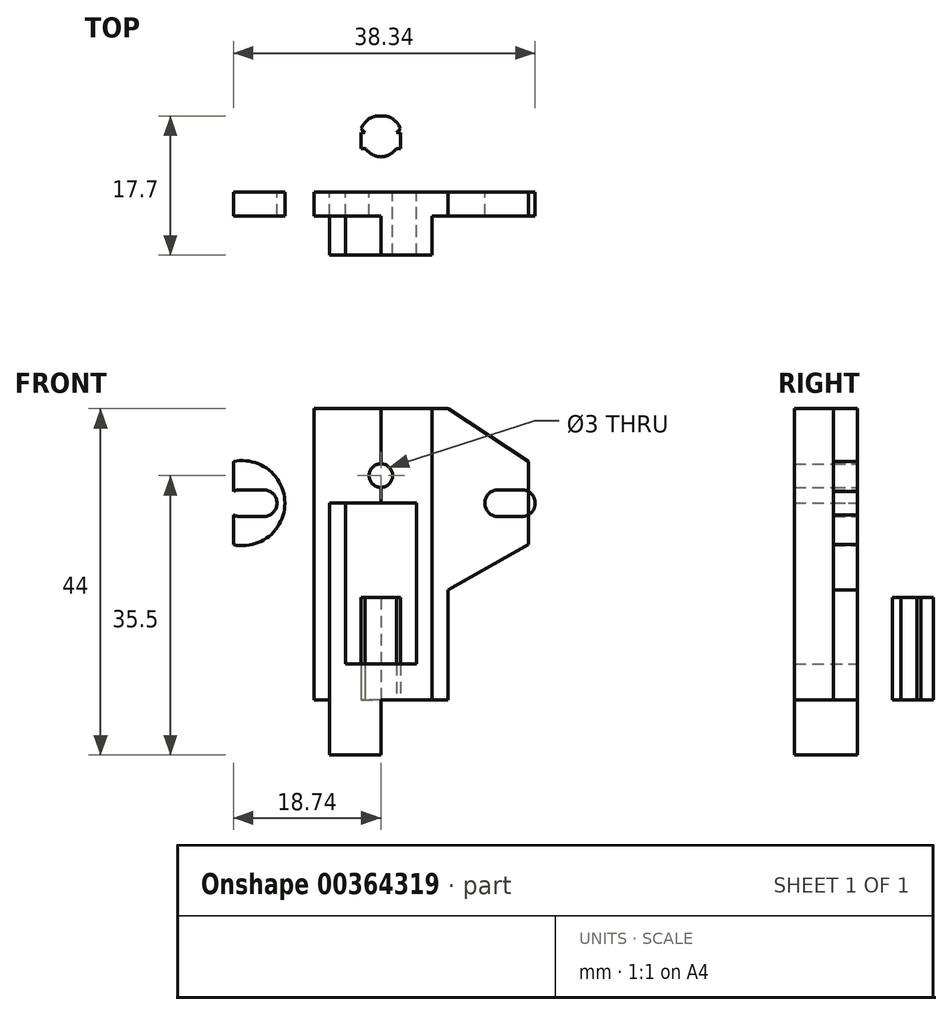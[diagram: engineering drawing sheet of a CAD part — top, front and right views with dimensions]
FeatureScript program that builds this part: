
annotation { "Feature Type Name" : "Feature", "Feature Type Description" : "" }
export const myFeature = defineFeature(function(context is Context, id is Id, definition is map)
    precondition{}
    {
        {
            var Q0;
            Q0=qCreatedBy(makeId("Front.planeOp"),FACE);
            var sketch = newSketch(context, id + "F0", { "sketchPlane" : qUnion([Q0])});
            skLineSegment(sketch, "E0.bottom", {"start": v(0, 0) * mm, "end": v(-8.5, 0) * mm});
            skLineSegment(sketch, "E0.top", {"start": v(0, 37) * mm, "end": v(-8.5, 37) * mm});
            skLineSegment(sketch, "E0.left", {"start": v(0, 0) * mm, "end": v(0, 37) * mm});
            skLineSegment(sketch, "E0.right", {"start": v(-8.5, 0) * mm, "end": v(-8.5, 37) * mm});
            skCircle(sketch, "E1", {"center": v(-17.6, 25) * mm, "radius": 5.4 * mm});
            skLineSegment(sketch, "E2", {"start": v(-8.5, 14) * mm, "end": v(-8.5, 37) * mm});
            skLineSegment(sketch, "E3", {"start": v(-8.5, 37) * mm, "end": v(-18.74, 30.28) * mm});
            skLineSegment(sketch, "E4", {"start": v(-18.74, 30.28) * mm, "end": v(-18.74, 19.72) * mm});
            skLineSegment(sketch, "E5", {"start": v(-18.74, 19.72) * mm, "end": v(-8.5, 14) * mm});
            skLineSegment(sketch, "E6.bottom", {"start": v(0, 37) * mm, "end": v(-6.5, 37) * mm});
            skLineSegment(sketch, "E6.top", {"start": v(0, -7) * mm, "end": v(-6.5, -7) * mm});
            skLineSegment(sketch, "E6.left", {"start": v(0, 37) * mm, "end": v(0, -7) * mm});
            skLineSegment(sketch, "E6.right", {"start": v(-6.5, 37) * mm, "end": v(-6.5, -7) * mm});
            skLineSegment(sketch, "E7.bottom", {"start": v(-6.5, 37) * mm, "end": v(0, 37) * mm});
            skLineSegment(sketch, "E7.top", {"start": v(-6.5, 25) * mm, "end": v(0, 25) * mm});
            skLineSegment(sketch, "E7.left", {"start": v(-6.5, 37) * mm, "end": v(-6.5, 25) * mm});
            skLineSegment(sketch, "E7.right", {"start": v(0, 37) * mm, "end": v(0, 25) * mm});
            skLineSegment(sketch, "E8.bottom", {"start": v(-6.5, -7) * mm, "end": v(0, -7) * mm});
            skLineSegment(sketch, "E8.top", {"start": v(-6.5, 4.6) * mm, "end": v(0, 4.6) * mm});
            skLineSegment(sketch, "E8.left", {"start": v(-6.5, -7) * mm, "end": v(-6.5, 4.6) * mm});
            skLineSegment(sketch, "E8.right", {"start": v(0, -7) * mm, "end": v(0, 4.6) * mm});
            skLineSegment(sketch, "E9.bottom", {"start": v(0, 25) * mm, "end": v(-4.5, 25) * mm});
            skLineSegment(sketch, "E9.top", {"start": v(0, 4.6) * mm, "end": v(-4.5, 4.6) * mm});
            skLineSegment(sketch, "E9.left", {"start": v(0, 25) * mm, "end": v(0, 4.6) * mm});
            skLineSegment(sketch, "E9.right", {"start": v(-4.5, 25) * mm, "end": v(-4.5, 4.6) * mm});
            skLineSegment(sketch, "E10.MirrorCS", {"start": v(6.5, 4.6) * mm, "end": v(0, 4.6) * mm});
            skLineSegment(sketch, "E11.MirrorCS", {"start": v(0, 4.6) * mm, "end": v(4.5, 4.6) * mm});
            skLineSegment(sketch, "E12.MirrorCS", {"start": v(6.5, 37) * mm, "end": v(0, 37) * mm});
            skLineSegment(sketch, "E13.MirrorCS", {"start": v(6.5, 25) * mm, "end": v(0, 25) * mm});
            skLineSegment(sketch, "E14.MirrorCS", {"start": v(0, 25) * mm, "end": v(4.5, 25) * mm});
            skLineSegment(sketch, "E15.MirrorCS", {"start": v(0, 37) * mm, "end": v(8.5, 37) * mm});
            skLineSegment(sketch, "E16.MirrorCS", {"start": v(6.5, -7) * mm, "end": v(6.5, 4.6) * mm});
            skLineSegment(sketch, "E17.MirrorCS", {"start": v(6.5, -7) * mm, "end": v(0, -7) * mm});
            skLineSegment(sketch, "E18.MirrorCS", {"start": v(6.5, 37) * mm, "end": v(6.5, 25) * mm});
            skLineSegment(sketch, "E19.MirrorCS", {"start": v(4.5, 25) * mm, "end": v(4.5, 4.6) * mm});
            skCircle(sketch, "E20.MirrorC", {"center": v(17.6, 25) * mm, "radius": 5.4 * mm});
            skLineSegment(sketch, "E21.MirrorCS", {"start": v(8.5, 14) * mm, "end": v(8.5, 37) * mm});
            skLineSegment(sketch, "E22.MirrorCS", {"start": v(0, -7) * mm, "end": v(6.5, -7) * mm});
            skLineSegment(sketch, "E23.MirrorCS", {"start": v(0, 37) * mm, "end": v(6.5, 37) * mm});
            skLineSegment(sketch, "E24.MirrorCS", {"start": v(8.5, 0) * mm, "end": v(8.5, 37) * mm});
            skLineSegment(sketch, "E25.MirrorCS", {"start": v(0, 0) * mm, "end": v(8.5, 0) * mm});
            skLineSegment(sketch, "E26.MirrorCS", {"start": v(6.5, 37) * mm, "end": v(6.5, -7) * mm});
            skLineSegment(sketch, "E27.MirrorCS", {"start": v(18.74, 19.72) * mm, "end": v(8.5, 14) * mm});
            skLineSegment(sketch, "E28.MirrorCS", {"start": v(18.74, 30.28) * mm, "end": v(18.74, 19.72) * mm});
            skLineSegment(sketch, "E29.MirrorCS", {"start": v(8.5, 37) * mm, "end": v(18.74, 30.28) * mm});
            skCircle(sketch, "E30", {"center": v(-17.9, 25) * mm, "radius": 1.7 * mm});
            skPoint(sketch, "E30.first.point", {"position": v(-17.9, 26.7) * mm});
            skPoint(sketch, "E30.second.point", {"position": v(-17.9, 23.3) * mm});
            skPoint(sketch, "E30.third.point", {"position": v(-19.6, 25) * mm});
            skCircle(sketch, "E31", {"center": v(-14.9, 25) * mm, "radius": 1.7 * mm});
            skPoint(sketch, "E31.first.point", {"position": v(-14.9, 26.7) * mm});
            skPoint(sketch, "E31.second.point", {"position": v(-14.9, 23.3) * mm});
            skPoint(sketch, "E31.third.point", {"position": v(-13.2, 25) * mm});
            skLineSegment(sketch, "E32", {"start": v(-17.9, 26.7) * mm, "end": v(-14.9, 26.7) * mm});
            skLineSegment(sketch, "E33", {"start": v(-17.9, 23.3) * mm, "end": v(-14.9, 23.3) * mm});
            skLineSegment(sketch, "E34.MirrorCS", {"start": v(17.9, 26.7) * mm, "end": v(14.9, 26.7) * mm});
            skLineSegment(sketch, "E35.MirrorCS", {"start": v(17.9, 23.3) * mm, "end": v(14.9, 23.3) * mm});
            skCircle(sketch, "E36.MirrorC", {"center": v(14.9, 25) * mm, "radius": 1.7 * mm});
            skCircle(sketch, "E37.MirrorC", {"center": v(17.9, 25) * mm, "radius": 1.7 * mm});
            skCircle(sketch, "E38", {"center": v(0, 18.3) * mm, "radius": 1.7 * mm});
            skPoint(sketch, "E38.first.point", {"position": v(0, 20) * mm});
            skPoint(sketch, "E38.second.point", {"position": v(-1.63, 17.83) * mm});
            skPoint(sketch, "E38.third.point", {"position": v(1.63, 17.83) * mm});
            skCircle(sketch, "E39", {"center": v(0, 18.3) * mm, "radius": 3.2 * mm});
            skCircle(sketch, "E40", {"center": v(0, 28.5) * mm, "radius": 1.5 * mm});
            skSolve(sketch);
        }
        {
            var Q0;
            {var subQ1=sQuery(id+"F0.wireOp",EDGE,"E7.bottom");Q0=makeQuery(id+"F0.imprint","IMPRINT",FACE,{"disambiguationData":[TD([[makeQuery(id+"F0.imprint","IMPRINT",EDGE,{"derivedFrom":subQ1}),-1.0]])]});}
            var Q1;
            {var subQ6=sQuery(id+"F0.wireOp",EDGE,"E13.MirrorCS");Q1=makeQuery(id+"F0.imprint","IMPRINT",FACE,{"disambiguationData":[TD([[makeQuery(id+"F0.imprint","IMPRINT",EDGE,{"derivedFrom":subQ6}),-1.0]])]});}
            var Q2;
            {var subQ0=sQuery(id+"F0.wireOp",EDGE,"E10.MirrorCS");Q2=makeQuery(id+"F0.imprint","IMPRINT",FACE,{"disambiguationData":[TD([[makeQuery(id+"F0.imprint","IMPRINT",EDGE,{"derivedFrom":subQ0}),-1.0]])]});}
            var Q3;
            {var subQ5=sQuery(id+"F0.wireOp",EDGE,"E10.MirrorCS");Q3=makeQuery(id+"F0.imprint","IMPRINT",FACE,{"disambiguationData":[TD([[makeQuery(id+"F0.imprint","IMPRINT",EDGE,{"derivedFrom":subQ5}),1.0]])]});}
            var Q4;
            {var subQ5=sQuery(id+"F0.wireOp",EDGE,"E8.top");Q4=makeQuery(id+"F0.imprint","IMPRINT",FACE,{"disambiguationData":[TD([[makeQuery(id+"F0.imprint","IMPRINT",EDGE,{"derivedFrom":subQ5}),-1.0]])]});}
            var Q5;
            {var subQ5=sQuery(id+"F0.wireOp",EDGE,"E8.bottom");Q5=makeQuery(id+"F0.imprint","IMPRINT",FACE,{"disambiguationData":[TD([[makeQuery(id+"F0.imprint","IMPRINT",EDGE,{"derivedFrom":subQ5}),1.0]])]});}
            var Q6;
            {var subQ3=sQuery(id+"F0.wireOp",EDGE,"E22.MirrorCS");Q6=makeQuery(id+"F0.imprint","IMPRINT",FACE,{"disambiguationData":[TD([[makeQuery(id+"F0.imprint","IMPRINT",EDGE,{"derivedFrom":subQ3}),1.0]])]});}
            var Q7;
            Q7=makeQuery(id+"F0.imprint","IMPRINT",FACE,{"disambiguationData":[TD([[makeQuery(id+"F0.imprint","IMPRINT",EDGE,{"derivedFrom":sQuery(id+"F0.wireOp",EDGE,"E6.right")}),1.0]])]});
            extrude(context, id + "F1", {"entities" : qUnion([Q0, Q1, Q2, Q3, Q4, Q5, Q6, Q7]), "depth" : 8 * mm});
        }
        {
            var Q0;
            Q0=makeQuery(id+"F0.imprint","IMPRINT",FACE,{"disambiguationData":[TD([[makeQuery(id+"F0.imprint","IMPRINT",EDGE,{"derivedFrom":sQuery(id+"F0.wireOp",EDGE,"E0.top")}),1.0]])]});
            var Q1;
            Q1=makeQuery(id+"F0.imprint","IMPRINT",FACE,{"disambiguationData":[TD([[makeQuery(id+"F0.imprint","IMPRINT",EDGE,{"derivedFrom":sQuery(id+"F0.wireOp",EDGE,"E2")}),1.0]])]});
            var Q2;
            {var subQ1=sQuery(id+"F0.wireOp",EDGE,"E9.bottom");Q2=makeQuery(id+"F0.imprint","IMPRINT",FACE,{"disambiguationData":[TD([[makeQuery(id+"F0.imprint","IMPRINT",EDGE,{"derivedFrom":subQ1}),1.0]])]});}
            var Q3;
            {var subQ4=sQuery(id+"F0.wireOp",EDGE,"E11.MirrorCS");Q3=makeQuery(id+"F0.imprint","IMPRINT",FACE,{"disambiguationData":[TD([[makeQuery(id+"F0.imprint","IMPRINT",EDGE,{"derivedFrom":subQ4}),1.0]])]});}
            var Q4;
            {var subQ1=sQuery(id+"F0.wireOp",EDGE,"E27.MirrorCS");Q4=makeQuery(id+"F0.imprint","IMPRINT",FACE,{"disambiguationData":[TD([[makeQuery(id+"F0.imprint","IMPRINT",EDGE,{"derivedFrom":subQ1}),-1.0]])]});}
            var Q5;
            {var subQ5=sQuery(id+"F0.wireOp",EDGE,"E15.MirrorCS");Q5=makeQuery(id+"F0.imprint","IMPRINT",FACE,{"disambiguationData":[TD([[makeQuery(id+"F0.imprint","IMPRINT",EDGE,{"derivedFrom":subQ5}),-1.0]])]});}
            var Q6;
            {var subQ0=sQuery(id+"F0.wireOp",EDGE,"E32");Q6=makeQuery(id+"F0.imprint","IMPRINT",FACE,{"disambiguationData":[TD([[makeQuery(id+"F0.imprint","IMPRINT",EDGE,{"derivedFrom":subQ0}),1.0]])]});}
            var Q7;
            {var subQ0=sQuery(id+"F0.wireOp",EDGE,"E4");var subQ4=sQuery(id+"F0.wireOp",EDGE,"E30");var subQ5=makeQuery(id+"F0.imprint","INTERSECT",VERTEX,{"disambiguationData":[OD(0.0)],"derivedFrom":[subQ0,subQ4]});Q7=makeQuery(id+"F0.imprint","IMPRINT",FACE,{"disambiguationData":[TD([[makeQuery(id+"F0.imprint","IMPRINT",EDGE,{"disambiguationData":[TD([[subQ5,-1.0]])],"derivedFrom":subQ4}),-1.0]])]});}
            var Q8;
            {var subQ0=sQuery(id+"F0.wireOp",EDGE,"E28.MirrorCS");var subQ4=sQuery(id+"F0.wireOp",EDGE,"E37.MirrorC");var subQ6=makeQuery(id+"F0.imprint","INTERSECT",VERTEX,{"disambiguationData":[OD(0.0)],"derivedFrom":[subQ0,subQ4]});Q8=makeQuery(id+"F0.imprint","IMPRINT",FACE,{"disambiguationData":[TD([[makeQuery(id+"F0.imprint","IMPRINT",EDGE,{"disambiguationData":[TD([[subQ6,-1.0]])],"derivedFrom":subQ4}),1.0]])]});}
            var Q9;
            {var subQ0=sQuery(id+"F0.wireOp",EDGE,"E34.MirrorCS");Q9=makeQuery(id+"F0.imprint","IMPRINT",FACE,{"disambiguationData":[TD([[makeQuery(id+"F0.imprint","IMPRINT",EDGE,{"derivedFrom":subQ0}),-1.0]])]});}
            var Q10;
            {var subQ0=sQuery(id+"F0.wireOp",EDGE,"E39");var subQ1=sQuery(id+"F0.wireOp",EDGE,"E9.left");var subQ2=makeQuery(id+"F0.imprint","INTERSECT",VERTEX,{"disambiguationData":[OD(0.0)],"derivedFrom":[subQ1,subQ0]});Q10=makeQuery(id+"F0.imprint","IMPRINT",FACE,{"disambiguationData":[TD([[makeQuery(id+"F0.imprint","IMPRINT",EDGE,{"disambiguationData":[TD([[subQ2,-1.0]])],"derivedFrom":subQ1}),1.0]])]});}
            var Q11;
            {var subQ0=sQuery(id+"F0.wireOp",EDGE,"E39");var subQ1=sQuery(id+"F0.wireOp",EDGE,"E9.left");var subQ2=makeQuery(id+"F0.imprint","INTERSECT",VERTEX,{"disambiguationData":[OD(0.0)],"derivedFrom":[subQ1,subQ0]});Q11=makeQuery(id+"F0.imprint","IMPRINT",FACE,{"disambiguationData":[TD([[makeQuery(id+"F0.imprint","IMPRINT",EDGE,{"disambiguationData":[TD([[subQ2,-1.0]])],"derivedFrom":subQ1}),-1.0]])]});}
            extrude(context, id + "F2", {"entities" : qUnion([Q0, Q1, Q2, Q3, Q4, Q5, Q6, Q7, Q8, Q9, Q10, Q11]), "operationType" : NewBodyOperationType.ADD, "depth" : 3 * mm});
        }
        {
            var Q0;
            Q0=qCreatedBy(makeId("Top.planeOp"),FACE);
            var sketch = newSketch(context, id + "F3", { "sketchPlane" : qUnion([Q0])});
            skFitSpline(sketch, "E41", {"points": [v(0, 4.5) * mm, v(-1.15, 4.84) * mm, v(-2, 5.57) * mm], "startDerivative": vector(-2.92, 0) * mm, "endDerivative": vector(-2.13, 2.71) * mm});
            skLineSegment(sketch, "E42", {"start": v(-2, 5.57) * mm, "end": v(-2.5, 5.57) * mm});
            skLineSegment(sketch, "E43", {"start": v(-2.5, 5.57) * mm, "end": v(-2.5, 7.57) * mm});
            skLineSegment(sketch, "E44", {"start": v(-2.5, 7.57) * mm, "end": v(-2, 7.57) * mm});
            skLineSegment(sketch, "E45", {"start": v(-2, 7.57) * mm, "end": v(-2.5, 8.08) * mm});
            skFitSpline(sketch, "E46", {"points": [v(-2.5, 8.08) * mm, v(-2, 8.86) * mm, v(-1.67, 9.18) * mm, v(-1.23, 9.48) * mm, v(0, 9.7) * mm], "startDerivative": vector(2.56, 4.92) * mm, "endDerivative": vector(6.54, 0.25) * mm});
            skFitSpline(sketch, "E47.MirrorCS", {"points": [v(0, 4.5) * mm, v(1.15, 4.84) * mm, v(2, 5.57) * mm], "startDerivative": vector(2.92, 0) * mm, "endDerivative": vector(2.13, 2.71) * mm});
            skLineSegment(sketch, "E48.MirrorCS", {"start": v(2, 5.57) * mm, "end": v(2.5, 5.57) * mm});
            skLineSegment(sketch, "E49.MirrorCS", {"start": v(2.5, 7.57) * mm, "end": v(2, 7.57) * mm});
            skLineSegment(sketch, "E50.MirrorCS", {"start": v(2, 7.57) * mm, "end": v(2.5, 8.08) * mm});
            skLineSegment(sketch, "E51.MirrorCS", {"start": v(2.5, 5.57) * mm, "end": v(2.5, 7.57) * mm});
            skFitSpline(sketch, "E52.MirrorCS", {"points": [v(2.5, 8.08) * mm, v(2, 8.86) * mm, v(1.67, 9.18) * mm, v(1.23, 9.48) * mm, v(0, 9.7) * mm], "startDerivative": vector(-2.56, 4.92) * mm, "endDerivative": vector(-6.54, 0.25) * mm});
            skSolve(sketch);
        }
        {
            var Q0;
            Q0=makeQuery(id+"F3.imprint","IMPRINT",FACE,{"disambiguationData":[TD([[makeQuery(id+"F3.imprint","IMPRINT",EDGE,{"derivedFrom":sQuery(id+"F3.wireOp",EDGE,"E41")}),-1.0]])]});
            extrude(context, id + "F4", {"entities" : qUnion([Q0]), "depth" : 13 * mm});
        }
    });
